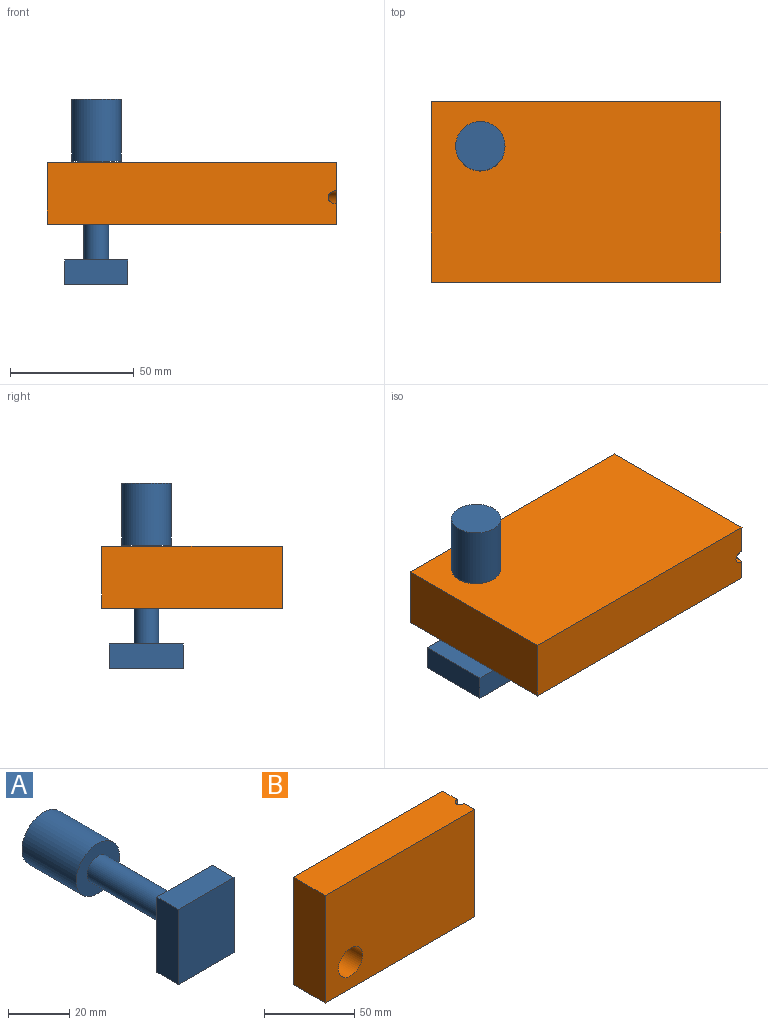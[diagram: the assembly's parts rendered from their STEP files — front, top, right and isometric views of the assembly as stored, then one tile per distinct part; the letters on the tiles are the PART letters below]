
ASSEMBLY  parts=2 mates=1
PART A: 10 faces, bbox 25.5x75x30 mm
  f0: cylinder r=10mm len=25mm, axis (0,1,0), area 1570.8mm2, adj f1,f2
  f1: plane 20x20mm, normal (0,-1,0), area 235.6mm2, adj f0,f3
  f2: plane 20x20mm, normal (0,1,0), area 314.2mm2, adj f0
  f3: cylinder r=5mm len=40mm, axis (0,1,0), area 1256.6mm2, adj f1,f9
  f4: plane 30x10mm, normal (1,0,0), area 300mm2, adj f5,f7,f8,f9
  f5: plane 25.54x10mm, normal (0,0,1), area 255.4mm2, adj f4,f6,f8,f9
  f6: plane 30x10mm, normal (-1,0,0), area 300mm2, adj f5,f7,f8,f9
  f7: plane 25.54x10mm, normal (0,0,-1), area 255.4mm2, adj f4,f6,f8,f9
  f8: plane 30x25.54mm, normal (0,-1,0), area 766.1mm2, adj f4,f5,f6,f7
  f9: plane 30x25.54mm, normal (0,1,0), area 687.5mm2, adj f3,f4,f5,f6,f7
PART B: 8 faces, bbox 119.2x25x78.5 mm
  f0: plane 72.9x25mm, normal (1,0,0), area 1803.3mm2, adj f1,f3,f4,f5,f6
  f1: plane 117x25mm, normal (0,0,1), area 2910.6mm2, adj f0,f2,f4,f5,f6
  f2: plane 72.9x25mm, normal (-1,0,0), area 1822.5mm2, adj f1,f3,f4,f5
  f3: plane 117x25mm, normal (0,0,-1), area 2891.4mm2, adj f0,f2,f4,f5,f6
  f4: plane 117x72.9mm, normal (0,-1,0), area 8245.8mm2, adj f0,f1,f2,f3,f7
  f5: plane 117x72.9mm, normal (0,1,0), area 8245.8mm2, adj f0,f1,f2,f3,f7
  f6: cylinder r=2.75mm len=78.54mm, axis (0.71,0,0.71), area 1745.6mm2, adj f0,f1,f3
  f7: cylinder r=9.5mm len=25mm, axis (0,-1,0), area 1492.3mm2, adj f4,f5
PLACE A rot(axis=(1,0,0),90deg) t=(-95.2,32.58,64.64)mm
PLACE B rot(axis=(1,0,0),90deg) t=(-84.1,-9.72,39.12)mm
MATE cylindrical A.f0 <-> B.f7  axis (0,0,1) through (-123.85,5.88,64.64)mm
